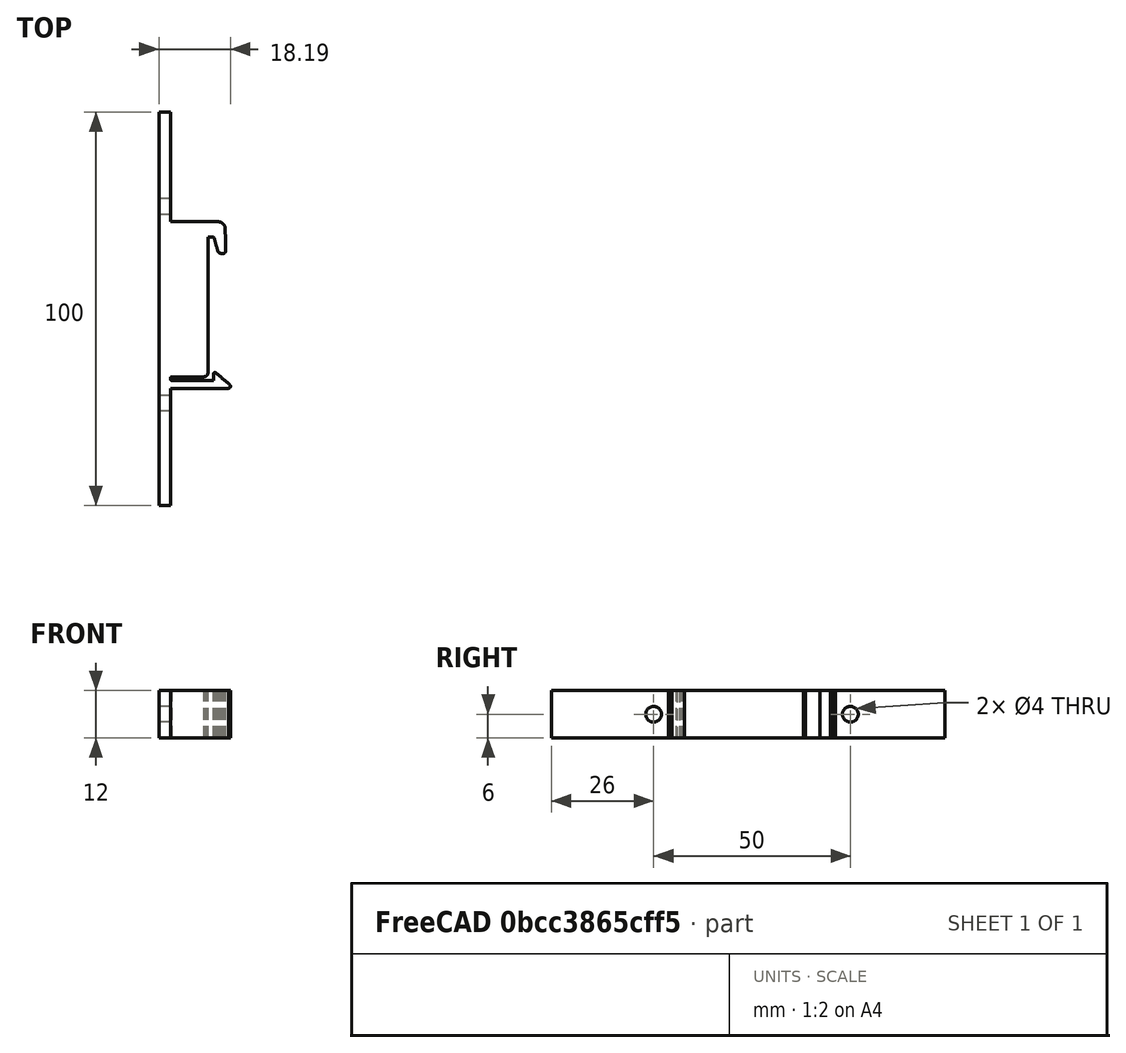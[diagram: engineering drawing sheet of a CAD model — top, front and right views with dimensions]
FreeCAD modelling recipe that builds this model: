
FCSTD DOCUMENT  (FreeCAD 0.18.4R)
Label: dinrail_mw_lrs200
License: All rights reserved
LicenseURL: http://en.wikipedia.org/wiki/All_rights_reserved
objects: Part::Feature×2, Sketcher::SketchObject×2, Mesh::Feature×1, PartDesign::FeatureBase×1, PartDesign::Pad×1, PartDesign::Hole×1, PartDesign::SubtractiveBox×1, PartDesign::Body×1
note: 12 computed .brp shape members not serialized (recipe doc carries the construction recipe); baked Part::Feature solids carry a one-line shape summary decoded from their .brp

FEATURE [Mesh::Feature] pcb_din_clip_mph
FEATURE [Part::Feature] pcb_din_clip_mph001
  shape: bbox 22.19 x 66 x 6 mm, 284 faces, 0 solids (baked)
FEATURE [Part::Feature] Solid
  Placement = pos=(30,0,0) rot=(0,0,1;0rad)
  shape: bbox 22.19 x 66 x 12 mm, 72 faces (baked)
FEATURE [Sketcher::SketchObject] Sketch
  AttachmentOffset = pos=(0,0,1) rot=(0,0,1;0rad)
  MapMode = 5
  Placement = pos=(1,-2e-16,2e-16) rot=(0.57735,0.57735,0.57735;2.0944rad)
  Support = -> [YZ_Plane]
  sketch-geometry (4):
    g0: LineSegment StartX=-50 StartY=6 StartZ=0 EndX=50 EndY=6 EndZ=0
    g1: LineSegment StartX=50 StartY=6 StartZ=0 EndX=50 EndY=-6 EndZ=0
    g2: LineSegment StartX=50 StartY=-6 StartZ=0 EndX=-50 EndY=-6 EndZ=0
    g3: LineSegment StartX=-50 StartY=-6 StartZ=0 EndX=-50 EndY=6 EndZ=0
  constraints (12):
    c: Coincident(g0,g1)
    c: Coincident(g1,g2)
    c: Coincident(g2,g3)
    c: Coincident(g3,g0)
    c: Horizontal(g0)
    c: Horizontal(g2)
    c: Vertical(g1)
    c: Vertical(g3)
    c: DistanceX(g0,g0) = 100
    c: DistanceY(g1,g1) = 12
    c: DistanceX(g0,g-1) = 50
    c: DistanceY(g2,g-1) = 6
FEATURE [PartDesign::FeatureBase] BaseFeature
  BaseFeature = -> Solid
FEATURE [PartDesign::Pad] Pad  label="Long Plate Pad"
  BaseFeature = -> BaseFeature
  Length = 3
  Length2 = 100
  Profile = -> Sketch
  Type = 0
FEATURE [Sketcher::SketchObject] Sketch001  label=" Sketch001"
  Placement = pos=(4,0,0) rot=(0.57735,0.57735,0.57735;2.0944rad)
  Support = -> [YZ_Plane]
  sketch-geometry (2):
    g0: Circle CenterX=-24 CenterY=0 CenterZ=0 NormalX=0 NormalY=0 NormalZ=1 AngleXU=0 Radius=2
    g1: Circle CenterX=26 CenterY=0 CenterZ=0 NormalX=0 NormalY=0 NormalZ=1 AngleXU=0 Radius=2
  constraints (6):
    c: Diameter(g0) = 4
    c: Diameter(g1) = 4
    c: DistanceX(g0,g1) = 50
    c: DistanceX(g0,g-1) = 24
    c: Horizontal(g0,g-1)
    c: Horizontal(g-1,g1)
FEATURE [PartDesign::Hole] Hole  label="Screw Holes"
  BaseFeature = -> Pad
  Depth = 5
  DepthType = 0
  Diameter = 4
  DrillPoint = 1
  DrillPointAngle = 118
  HoleCutCountersinkAngle = 90
  HoleCutDepth = 0
  HoleCutDiameter = 0
  HoleCutType = 0
  ModelActualThread = false
  Profile = -> Sketch001
  Tapered = false
  TaperedAngle = 90
  ThreadAngle = 0
  ThreadClass = 0
  ThreadCutOffInner = 0
  ThreadCutOffOuter = 0
  ThreadDirection = 0
  ThreadFit = 0
  ThreadPitch = 0
  ThreadSize = 0
  ThreadType = 0
  Threaded = false
FEATURE [PartDesign::SubtractiveBox] Box
  AttacherType = Attacher::AttachEngine3D
  AttachmentOffset = pos=(-35,-6,-3) rot=(0,0,1;0rad)
  BaseFeature = -> Hole
  Height = 4
  Length = 70
  MapMode = 5
  Placement = pos=(-3,-35,-6) rot=(0.57735,0.57735,0.57735;2.0944rad)
  Support = -> [YZ_Plane]
  Width = 12
FEATURE [PartDesign::Body] Body
  BaseFeature = -> Solid
  Group = -> [BaseFeature,Sketch,Pad,Sketch001,Hole,Box]
  Origin = -> Origin
  Tip = -> Box
